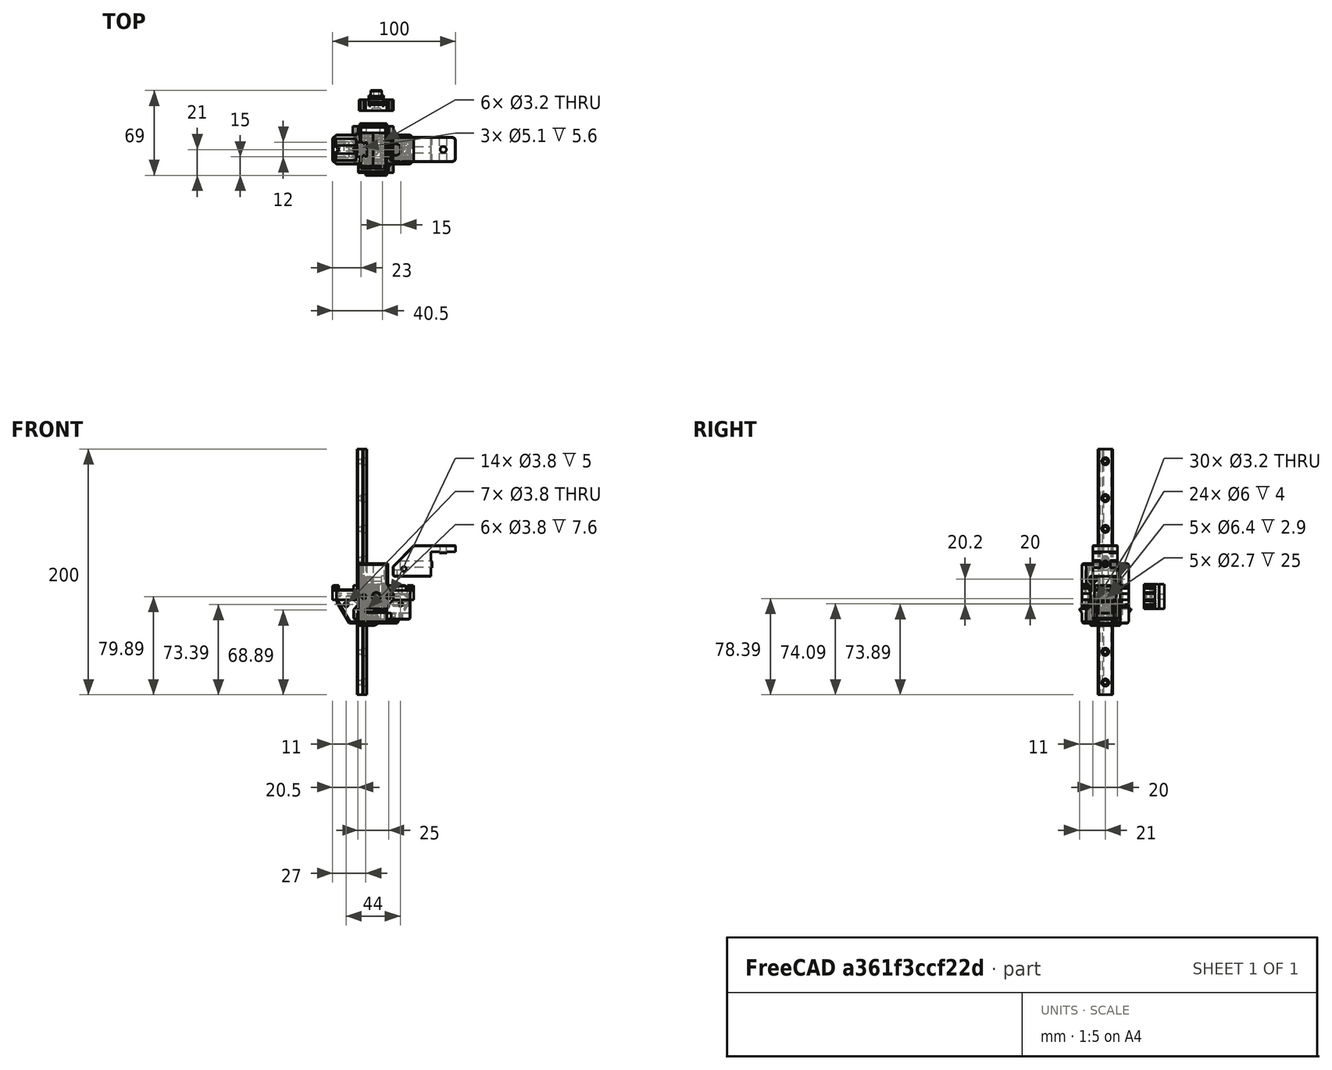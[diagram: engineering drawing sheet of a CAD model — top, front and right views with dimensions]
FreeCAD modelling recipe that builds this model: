
FCSTD DOCUMENT  (FreeCAD 0.19R24291 (Git))
Label: z-arm-threaded-ball
License: Other
LicenseURL: GPL3
objects: Part::Feature×26, Part::Chamfer×17, Part::Cut×16, Part::Cylinder×15, Part::Box×11, Part::MultiFuse×10, Part::Sphere×1, Part::MultiCommon×1
note: 97 computed .brp shape members not serialized (recipe doc carries the construction recipe); baked Part::Feature solids carry a one-line shape summary decoded from their .brp

FEATURE [Part::Box] Box048  label="Cube048"
  AttacherType = Attacher::AttachEngine3D
  Height = 8
  Length = 6
  Placement = pos=(10,-1.5,19.5) rot=(0,0,1;0rad)
  Width = 3
FEATURE [Part::Box] Box047  label="Cube047"
  AttacherType = Attacher::AttachEngine3D
  Height = 8
  Length = 3
  Placement = pos=(20.5,-9,19.5) rot=(0,0,1;0rad)
  Width = 3.25
FEATURE [Part::Box] Box046  label="Cube046"
  AttacherType = Attacher::AttachEngine3D
  Height = 8
  Length = 3
  Placement = pos=(28,-1.5,19.5) rot=(0,0,1;0rad)
  Width = 3
FEATURE [Part::Box] Box045  label="Cube045"
  AttacherType = Attacher::AttachEngine3D
  Height = 8
  Length = 3
  Placement = pos=(20.5,5.75,19.5) rot=(0,0,1;0rad)
  Width = 3.25
FEATURE [Part::Box] Box034  label="Cube034"
  AttacherType = Attacher::AttachEngine3D
  Height = 4
  Length = 10
  Placement = pos=(17,-12,23.5) rot=(0,0,1;0rad)
  Width = 3.85
FEATURE [Part::Feature] Cut028006004005002  label="block-base002"
  shape: bbox 28.5 x 37.5 x 48.4 mm, 58 faces (baked)
FEATURE [Part::Cylinder] Cylinder023
  Angle = 360
  AttacherType = Attacher::AttachEngine3D
  Height = 28.3
  Placement = pos=(2e-16,0,17) rot=(0,1,0;1.5708rad)
  Radius = 1.35
FEATURE [Part::Box] Box036  label="Cube036"
  AttacherType = Attacher::AttachEngine3D
  Height = 4
  Length = 10
  Placement = pos=(30.15,5,23.5) rot=(0,0,-1;1.5708rad)
  Width = 2.85
FEATURE [Part::Feature] Chamfer004013007011015006009007001005003001
  shape: bbox 5.5 x 3 x 8 mm, 7 faces (baked)
FEATURE [Part::Box] Box035  label="Cube035"
  AttacherType = Attacher::AttachEngine3D
  Height = 4
  Length = 10
  Placement = pos=(17,8.15,23.5) rot=(0,0,1;0rad)
  Width = 3.85
FEATURE [Part::Feature] Cut028006004005011004001  label="supporter-rf001"
  shape: bbox 20 x 13 x 19 mm, 14 faces (baked)
FEATURE [Part::Feature] Cut028006004005001  label="block-base001"
  shape: bbox 28.5 x 37.5 x 48.4 mm, 58 faces (baked)
FEATURE [Part::Cylinder] Cylinder024
  Angle = 360
  AttacherType = Attacher::AttachEngine3D
  Height = 3.3
  Placement = pos=(2e-16,0,17) rot=(0,1,0;1.5708rad)
  Radius = 3.2
FEATURE [Part::MultiFuse] Fusion004025023  label="m3rf"
  Shapes = -> [Cylinder023,Cylinder024]
FEATURE [Part::Feature] Fusion004025023001  label="m3rf001"
  shape: bbox 28.3 x 6.4 x 6.4 mm, 6 faces (baked)
FEATURE [Part::MultiFuse] Fusion004025023014
  Shapes = -> [Box034,Box035]
FEATURE [Part::Chamfer] Chamfer004013007011015006009007001005003024
  Base = -> Fusion004025023014
  Edges = 4 edges r=1: [Edge2,Edge6,Edge14,Edge18]
FEATURE [Part::Feature] Cut028006004005011004002  label="supporter-rf002"
  shape: bbox 20 x 13 x 19 mm, 14 faces (baked)
FEATURE [Part::Chamfer] Chamfer004013007011015006009007001005003021
  Base = -> Box036
  Edges = 2 edges r=1: [Edge2,Edge6]
FEATURE [Part::Chamfer] Chamfer004013007011015006009007001005003022
  Base = -> Chamfer004013007011015006009007001005003021
  Edges = 5 edges r=0.4: [Edge3,Edge10,Edge14,Edge15,Edge16]
FEATURE [Part::Box] Box033  label="Cube033"
  AttacherType = Attacher::AttachEngine3D
  Height = 8
  Length = 5.5
  Placement = pos=(11,10.5,16) rot=(0,0,1;0rad)
  Width = 3
FEATURE [Part::Chamfer] Chamfer004013007011015006009007001005003
  Base = -> Box033
  Edges = 1 edges r=3: [Edge6]
FEATURE [Part::Chamfer] Chamfer004013007011015006009007001005003025
  Base = -> Chamfer004013007011015006009007001005003024
  Edges = 10 edges r=0.4: [Edge1,Edge5,Edge7,Edge8,Edge9,Edge21,Edge28,Edge32,Edge33,Edge34]
FEATURE [Part::Feature] Fusion004025023015006001  label="slider-slot-1016-bearing-x"
  shape: bbox 16.3 x 18.2 x 13.6 mm, 8 faces (baked)
FEATURE [Part::Feature] Fusion004025023015006002  label="slider-slot-1016-bearing-y"
  Placement = pos=(22,22,0) rot=(0,0,-1;1.5708rad)
  shape: bbox 18.2 x 16.3 x 13.6 mm, 8 faces (baked)
FEATURE [Part::Feature] Chamfer004013007011015006009007001005003027001  label="slider-base"
  shape: bbox 22 x 24 x 8 mm, 13 faces (baked)
FEATURE [Part::MultiFuse] Fusion
  Shapes = -> [Chamfer004013007011015006009007001005003022,Chamfer004013007011015006009007001005003027001]
FEATURE [Part::Cut] Cut
  Base = -> Fusion
  Tool = -> Fusion004025023015006001
FEATURE [Part::MultiFuse] Fusion004025023015006003
  Shapes = -> [Cut,Cut028006004005011004002,Cut028006004005002,Chamfer004013007011015006009007001005003001]
FEATURE [Part::Cut] Cut028006004005011004003001010002011
  Base = -> Fusion004025023015006003
  Tool = -> Fusion004025023
FEATURE [Part::Chamfer] Chamfer
  Base = -> Cut028006004005011004003001010002011
  Edges = 1 edges r=0.4: [Edge259]
FEATURE [Part::Chamfer] Chamfer004013007011015006009007001005003027002  label="x-slider-r3"
  Base = -> Chamfer
  Edges = 2 edges r=0.2: [Edge164,Edge166]
FEATURE [Part::Feature] Chamfer004013007011015006009007001005003027003  label="slider-base001"
  shape: bbox 22 x 24 x 8 mm, 13 faces (baked)
FEATURE [Part::Cut] Cut028006004005011004003001010002012
  Base = -> Chamfer004013007011015006009007001005003027003
  Tool = -> Fusion004025023015006002
FEATURE [Part::MultiFuse] Fusion004025023015006004
  Shapes = -> [Cut028006004005011004003001010002012,Chamfer004013007011015006009007001005003025,Cut028006004005001,Cut028006004005011004001,Chamfer004013007011015006009007001005003]
FEATURE [Part::Cut] Cut028006004005011004003001010002013
  Base = -> Fusion004025023015006004
  Tool = -> Fusion004025023001
FEATURE [Part::Chamfer] Chamfer004013007011015006009007001005003027004
  Base = -> Cut028006004005011004003001010002013
  Edges = 1 edges r=0.4: [Edge298]
FEATURE [Part::Chamfer] Chamfer004013007011015006009007001005003027005  label="y-slider-r3"
  Base = -> Chamfer004013007011015006009007001005003027004
  Edges = 2 edges r=0.2: [Edge162,Edge280]
FEATURE [Part::Feature] Chamfer004013007011015006009007001005003063003001002001002001001  label="1515-corner-arm-middle-threaded-ball"
  shape: bbox 31 x 20 x 20 mm, 68 faces (baked)
FEATURE [Part::Feature] Chamfer004013007011015006009007001005003063003001001  label="1515-corner-arm-front-threaded-ball"
  shape: bbox 46 x 20 x 20 mm, 99 faces (baked)
FEATURE [Part::Feature] Chamfer004013007011015006009007001005003063003001002001001  label="1515-corner-arm-back-threaded-ball"
  shape: bbox 46 x 20 x 20 mm, 111 faces (baked)
FEATURE [Part::Feature] Chamfer004013007011015006009007001005003062001  label="bed-mount-top-2020-threaded-ball001"
  shape: bbox 51 x 20 x 25 mm, 64 faces (baked)
FEATURE [Part::Cylinder] Cylinder
  Angle = 360
  AttacherType = Attacher::AttachEngine3D
  Height = 5
  Placement = pos=(22,0,35) rot=(0,0,1;0rad)
  Radius = 2.55
FEATURE [Part::Cut] Cut028006004005011004003001010002014
  Base = -> Chamfer004013007011015006009007001005003062001
  Tool = -> Cylinder
FEATURE [Part::Chamfer] Chamfer004013007011015006009007001005003063003001002001002001002  label="2020-arm"
  Base = -> Cut028006004005011004003001010002014
  Edges = 1 edges r=0.4: [Edge5]
FEATURE [Part::Cylinder] Cylinder025
  Angle = 360
  AttacherType = Attacher::AttachEngine3D
  Height = 6
  Placement = pos=(-10,0,0) rot=(0,0,1;0rad)
  Radius = 2.55
FEATURE [Part::Cylinder] Cylinder026
  Angle = 360
  AttacherType = Attacher::AttachEngine3D
  Height = 6
  Placement = pos=(-10,0,0) rot=(0,0,1;0rad)
  Radius = 2.55
FEATURE [Part::Cylinder] Cylinder027
  Angle = 360
  AttacherType = Attacher::AttachEngine3D
  Height = 6
  Placement = pos=(-10,0,0) rot=(0,0,1;0rad)
  Radius = 2.55
FEATURE [Part::Cut] Cut028006004005011004003001010002015
  Base = -> Chamfer004013007011015006009007001005003063003001002001002001001
  Tool = -> Cylinder025
FEATURE [Part::Chamfer] Chamfer004013007011015006009007001005003063003001002001002001003  label="1515-middle-arm"
  Base = -> Cut028006004005011004003001010002015
  Edges = 1 edges r=0.4: [Edge27]
FEATURE [Part::Cut] Cut028006004005011004003001010002016
  Base = -> Chamfer004013007011015006009007001005003063003001002001001
  Tool = -> Cylinder026
FEATURE [Part::Chamfer] Chamfer004013007011015006009007001005003063003001002001002001004  label="1515-back-arm"
  Base = -> Cut028006004005011004003001010002016
  Edges = 1 edges r=0.4: [Edge41]
FEATURE [Part::Cut] Cut028006004005011004003001010002017
  Base = -> Chamfer004013007011015006009007001005003063003001001
  Tool = -> Cylinder027
FEATURE [Part::Chamfer] Chamfer004013007011015006009007001005003063003001002001002001005  label="1515-front-arm"
  Base = -> Cut028006004005011004003001010002017
  Edges = 1 edges r=0.4: [Edge102]
FEATURE [Part::Cylinder] Cylinder028
  Angle = 360
  AttacherType = Attacher::AttachEngine3D
  Height = 2
  Radius = 4
FEATURE [Part::Cylinder] Cylinder029
  Angle = 360
  AttacherType = Attacher::AttachEngine3D
  Height = 2
  Radius = 2.1
FEATURE [Part::Cut] Cut028006004005011004003001010002018  label="spacer"
  Base = -> Cylinder028
  Tool = -> Cylinder029
FEATURE [Part::Cylinder] Cylinder030
  Angle = 360
  AttacherType = Attacher::AttachEngine3D
  Height = 8.5
  Radius = 3.5
FEATURE [Part::Cylinder] Cylinder031
  Angle = 360
  AttacherType = Attacher::AttachEngine3D
  Height = 8.5
  Radius = 1.7
FEATURE [Part::Cut] Cut028006004005011004003001010002019  label="bottom-spacer"
  Base = -> Cylinder030
  Tool = -> Cylinder031
FEATURE [Part::Cylinder] Cylinder032
  Angle = 360
  AttacherType = Attacher::AttachEngine3D
  Height = 5
  Radius = 1.7
FEATURE [Part::Cylinder] Cylinder033
  Angle = 360
  AttacherType = Attacher::AttachEngine3D
  Height = 5
  Radius = 3.5
FEATURE [Part::Cut] Cut028006004005011004003001010002020  label="top-spacer"
  Base = -> Cylinder033
  Tool = -> Cylinder032
FEATURE [Part::Sphere] Sphere
  Angle1 = -90
  Angle2 = 90
  Angle3 = 360
  AttacherType = Attacher::AttachEngine3D
  Radius = 5
FEATURE [Part::Cylinder] Cylinder034
  Angle = 360
  AttacherType = Attacher::AttachEngine3D
  Height = 10
  Placement = pos=(0,0,-1) rot=(0,0,1;0rad)
  Radius = 2
FEATURE [Part::Cut] Cut028006004005011004003001010002021
  Base = -> Sphere
  Tool = -> Cylinder034
FEATURE [Part::Chamfer] Chamfer004013007011015006009007001005003063003001002001002001006  label="10mm-thread-ball"
  Base = -> Cut028006004005011004003001010002021
  Edges = 1 edges r=0.4: [Edge1]
FEATURE [Part::Cylinder] Cylinder035
  Angle = 360
  AttacherType = Attacher::AttachEngine3D
  Height = 2
  Radius = 4
FEATURE [Part::Cylinder] Cylinder036
  Angle = 360
  AttacherType = Attacher::AttachEngine3D
  Height = 2
  Radius = 2.15
FEATURE [Part::Cut] Cut028006004005011004003001010002022
  Base = -> Cylinder035
  Tool = -> Cylinder036
FEATURE [Part::Chamfer] Chamfer004013007011015006009007001005003063003001002001002001007  label="threaded-ball-spacer"
  Base = -> Cut028006004005011004003001010002022
  Edges = 2 edges r=0.4: [Edge1,Edge4]
FEATURE [Part::Feature] Chamfer004013007011015006009007001005003063003001002001002001007001  label="threaded-ball-spacer001"
  shape: bbox 8 x 8 x 2 mm, 6 faces (baked)
FEATURE [Part::Box] Box054  label="Cube054"
  AttacherType = Attacher::AttachEngine3D
  Height = 54
  Length = 47
  Placement = pos=(-14,0,-7) rot=(0,0,1;0rad)
  Width = 25
FEATURE [Part::Feature] Fusion001001  label="_MGN12-pref"
  Placement = pos=(-7.5,4e-15,38.61) rot=(0,0,-1;1.5708rad)
  shape: bbox 13 x 27 x 200 mm, 427 faces (baked)
FEATURE [Part::Box] Box055  label="Cube055"
  AttacherType = Attacher::AttachEngine3D
  Height = 10
  Length = 13
  Placement = pos=(-13,-12,-5) rot=(0,0,1;0rad)
  Width = 24
FEATURE [Part::Chamfer] Chamfer004013007011015006009007001005003063003001002001002001007002  label="rail-bolt-cut-template"
  Base = -> Box055
  Edges = 2 edges r=5: [Edge5,Edge7]
FEATURE [Part::Feature] Chamfer004013007011015006009007001005003063003001002001002001007002001  label="rail-bolt-cut-template001"
  shape: bbox 13 x 24 x 10 mm, 8 faces (baked)
FEATURE [Part::Feature] Chamfer004013007011015006009007001005003063003001002001002001007002003  label="rail-bolt-cut-template003"
  shape: bbox 13 x 24 x 10 mm, 8 faces (baked)
FEATURE [Part::Cut] Cut028006004005011004003001010002023  label="x-slider-r4"
  Base = -> Chamfer004013007011015006009007001005003027002
  Tool = -> Chamfer004013007011015006009007001005003063003001002001002001007002001
FEATURE [Part::Cut] Cut028006004005011004003001010002024  label="y-slider-r4"
  Base = -> Chamfer004013007011015006009007001005003027005
  Tool = -> Chamfer004013007011015006009007001005003063003001002001002001007002003
FEATURE [Part::MultiFuse] Fusion004025023015006009  label="y-stopper"
  Shapes = -> [Box047,Box045]
FEATURE [Part::MultiFuse] Fusion004025023015006010  label="x-stopper"
  Shapes = -> [Box046,Box048]
FEATURE [Part::Feature] Cut028006004005011004003001010002024001  label="y-slider-r005"
  shape: bbox 45 x 37.5 x 48.4 mm, 142 faces (baked)
FEATURE [Part::Feature] Cut028006004005011004003001010002023001  label="x-slider-r005"
  shape: bbox 45 x 37.5 x 48.4 mm, 125 faces (baked)
FEATURE [Part::MultiFuse] Fusion004025023015006011  label="x-slider-r4-with-limiter"
  Shapes = -> [Fusion004025023015006010,Cut028006004005011004003001010002023001]
FEATURE [Part::MultiFuse] Fusion004025023015006012  label="y-slider-r4-with-limiter"
  Shapes = -> [Cut028006004005011004003001010002024001,Fusion004025023015006009]
FEATURE [Part::Feature] Fusion004025023015006011001  label="x-slider-r4-with-limiter001"
  shape: bbox 45 x 37.5 x 48.4 mm, 138 faces (baked)
FEATURE [Part::MultiCommon] Common
  Shapes = -> [Box054,Fusion004025023015006011001]
FEATURE [Part::Feature] Part__Mirroring001  label="Common (Mirror #1)001"
  shape: bbox 45 x 21 x 48.4 mm, 95 faces (baked)
FEATURE [Part::MultiFuse] Fusion004025023015006011002  label="x-slider-r4-with-limiter-dual-mount"
  Shapes = -> [Common,Part__Mirroring001]
FEATURE [Part::Feature] Part__Mirroring002  label="x-slider-r4-with-limiter002 (Mirror #1)001"
  shape: bbox 45 x 37.5 x 48.4 mm, 138 faces (baked)
FEATURE [Part::Feature] Fusion003001  label="belt-holder"
  Placement = pos=(2.5,44,18.5) rot=(1,0,0;1.5708rad)
  shape: bbox 12 x 7 x 20 mm, 88 faces (baked)
FEATURE [Part::Box] Box031  label="Cube031"
  AttacherType = Attacher::AttachEngine3D
  Height = 6.4
  Length = 9.5
  Placement = pos=(-2.25,37.7,15.3) rot=(0,0,1;0rad)
  Width = 8
FEATURE [Part::Cut] Cut028006004005011004003  label="belt-mounter-9mm"
  Base = -> Fusion003001
  Tool = -> Box031
FEATURE [Part::Feature] Defeatured003
  shape: bbox 28 x 9 x 20 mm, 43 faces (baked)
FEATURE [Part::Feature] Cut002001  label="belt-clamp-nut"
  Placement = pos=(2.5,51.5,18.5) rot=(-1,0,0;1.5708rad)
  shape: bbox 9 x 5 x 20 mm, 11 faces (baked)
FEATURE [Part::Chamfer] Chamfer004013007011015006002  label="belt-connector-rf"
  Base = -> Defeatured003
  Edges = 4 edges r=1.5: [Edge18,Edge41,Edge42,Edge56]
